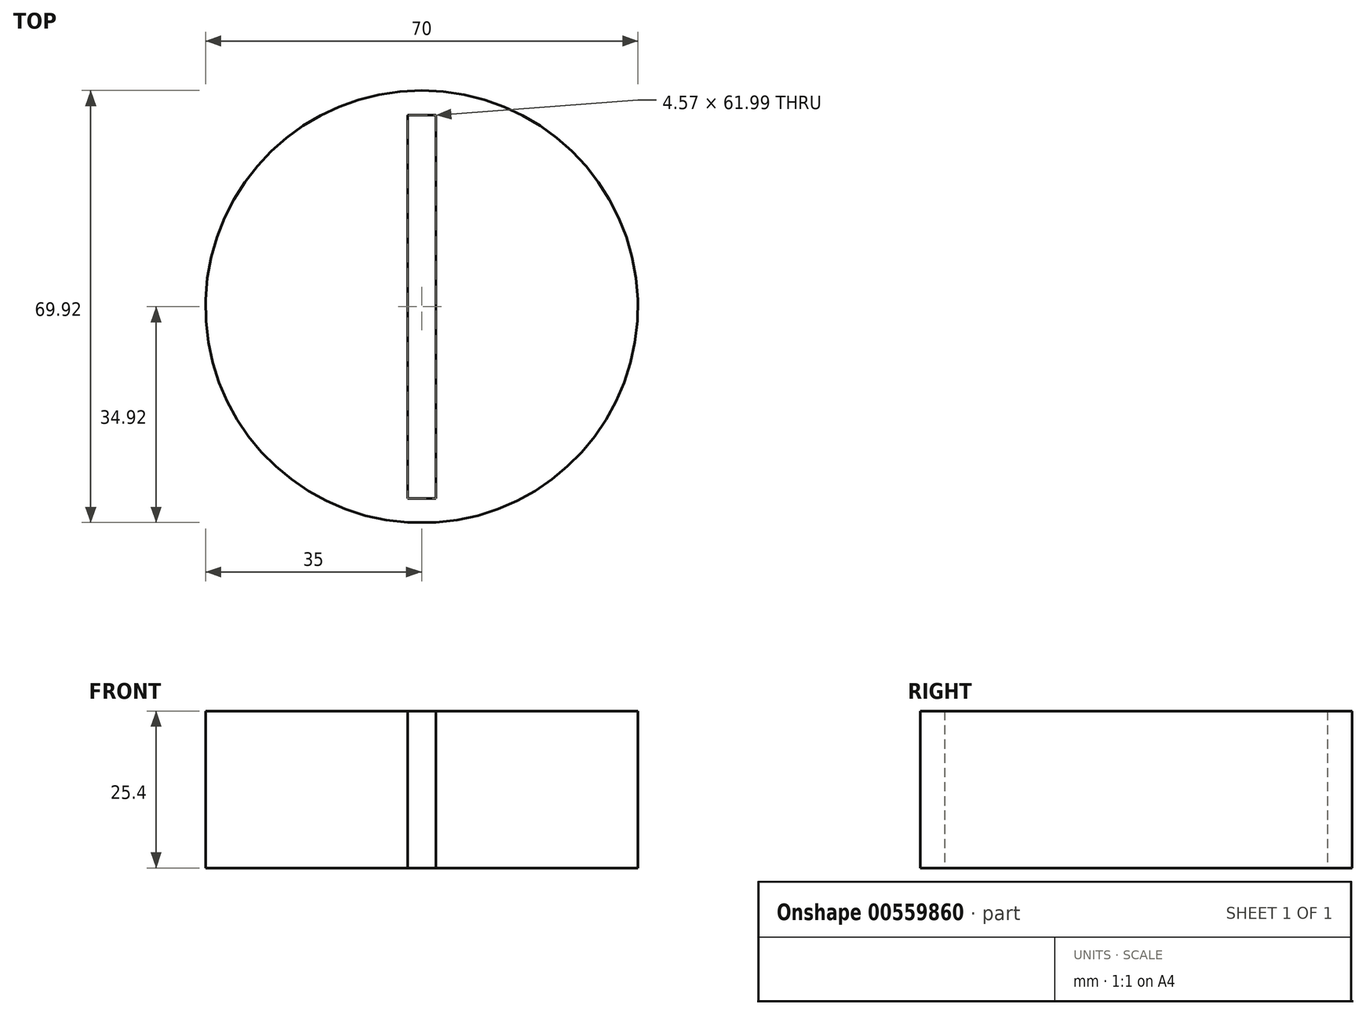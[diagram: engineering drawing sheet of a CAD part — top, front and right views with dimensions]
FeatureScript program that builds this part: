
annotation { "Feature Type Name" : "Feature", "Feature Type Description" : "" }
export const myFeature = defineFeature(function(context is Context, id is Id, definition is map)
    precondition{}
    {
        {
            var Q0;
            Q0=qCreatedBy(makeId("Top.planeOp"),FACE);
            var sketch = newSketch(context, id + "F0", { "sketchPlane" : qUnion([Q0])});
            skCircle(sketch, "E0", {"center": v(0, 0) * mm, "radius": 35 * mm});
            skLineSegment(sketch, "E1", {"start": v(2.29, 34.92) * mm, "end": v(2.29, -34.92) * mm});
            skLineSegment(sketch, "E2", {"start": v(2.29, -34.92) * mm, "end": v(-2.29, -34.92) * mm});
            skLineSegment(sketch, "E3", {"start": v(-2.29, -34.92) * mm, "end": v(-2.29, 34.92) * mm});
            skLineSegment(sketch, "E4", {"start": v(2.29, -31) * mm, "end": v(-2.29, -31) * mm});
            skLineSegment(sketch, "E5", {"start": v(-2.29, 31) * mm, "end": v(2.29, 31) * mm});
            skSolve(sketch);
        }
        {
            var Q0;
            {var subQ0=sQuery(id+"F0.wireOp",EDGE,"E3");Q0=makeQuery(id+"F0.imprint","IMPRINT",FACE,{"disambiguationData":[TD([[makeQuery(id+"F0.imprint","IMPRINT",EDGE,{"derivedFrom":subQ0}),1.0]])]});}
            var Q1;
            {var subQ0=sQuery(id+"F0.wireOp",EDGE,"E1");Q1=makeQuery(id+"F0.imprint","IMPRINT",FACE,{"disambiguationData":[TD([[makeQuery(id+"F0.imprint","IMPRINT",EDGE,{"derivedFrom":subQ0}),1.0]])]});}
            var Q2;
            {var subQ5=sQuery(id+"F0.wireOp",EDGE,"E5");Q2=makeQuery(id+"F0.imprint","IMPRINT",FACE,{"disambiguationData":[TD([[makeQuery(id+"F0.imprint","IMPRINT",EDGE,{"derivedFrom":subQ5}),1.0]])]});}
            var Q3;
            {var subQ0=sQuery(id+"F0.wireOp",EDGE,"E2");Q3=makeQuery(id+"F0.imprint","IMPRINT",FACE,{"disambiguationData":[TD([[makeQuery(id+"F0.imprint","IMPRINT",EDGE,{"derivedFrom":subQ0}),-1.0]])]});}
            extrude(context, id + "F1", {"entities" : qUnion([Q0, Q1, Q2, Q3]), "depth" : 25.4 * mm, "offsetDistance" : 25.4 * mm});
        }
    });
